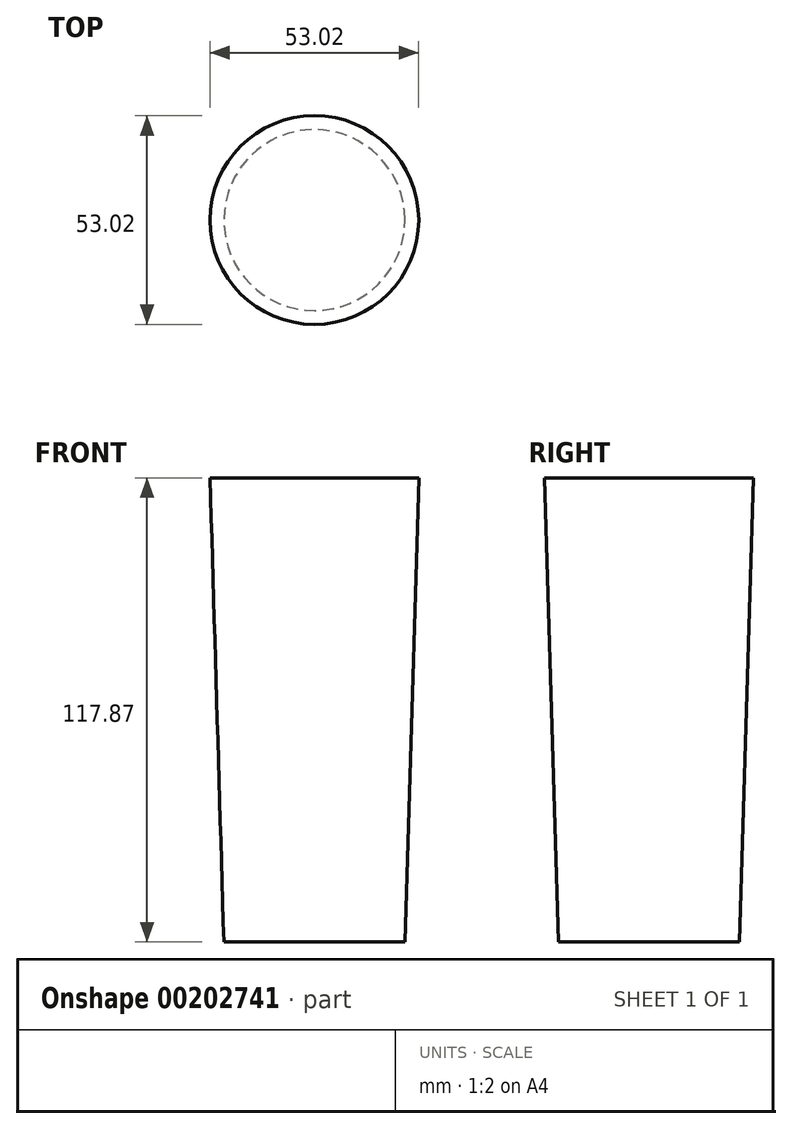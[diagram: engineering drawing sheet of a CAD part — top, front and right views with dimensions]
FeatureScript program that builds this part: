
annotation { "Feature Type Name" : "Feature", "Feature Type Description" : "" }
export const myFeature = defineFeature(function(context is Context, id is Id, definition is map)
    precondition{}
    {
        {
            var Q0;
            Q0=qCreatedBy(makeId("Front.planeOp"),FACE);
            var sketch = newSketch(context, id + "F0", { "sketchPlane" : qUnion([Q0])});
            skLineSegment(sketch, "E0", {"start": v(0, -154.16) * mm, "end": v(0, 45.84) * mm});
            skLineSegment(sketch, "E1", {"start": v(-28, 45.84) * mm, "end": v(-30, 45.84) * mm});
            skLineSegment(sketch, "E2.1", {"start": v(-28, 45.9) * mm, "end": v(-28, 45.84) * mm});
            skPoint(sketch, "E3.endSnap0", {"position": v(-25, -134.16) * mm});
            skLineSegment(sketch, "E4", {"start": v(-23, -134.16) * mm, "end": v(0, -134.16) * mm});
            skPoint(sketch, "E5.orphan", {"position": v(-25, -114.16) * mm});
            skPoint(sketch, "E6.start.orphan", {"position": v(-25, -154.16) * mm});
            skLineSegment(sketch, "E7", {"start": v(-26.51, -16.3) * mm, "end": v(-23, -134.16) * mm});
            skLineSegment(sketch, "E8", {"start": v(-26.51, -16.3) * mm, "end": v(0, -16.3) * mm});
            skPoint(sketch, "E9.start.orphan", {"position": v(-27, 0) * mm});
            skSolve(sketch);
        }
        {
            var Q0;
            Q0 = qSketchRegion(id + "F0", true);
            var Q1;
            Q1=sQuery(id+"F0.wireOp",EDGE,"E0");
            revolve(context, id + "F1", {"entities" : qUnion([Q0]), "axis" : qUnion([Q1]), "revolveType" : RevolveType.FULL});
        }
    });
